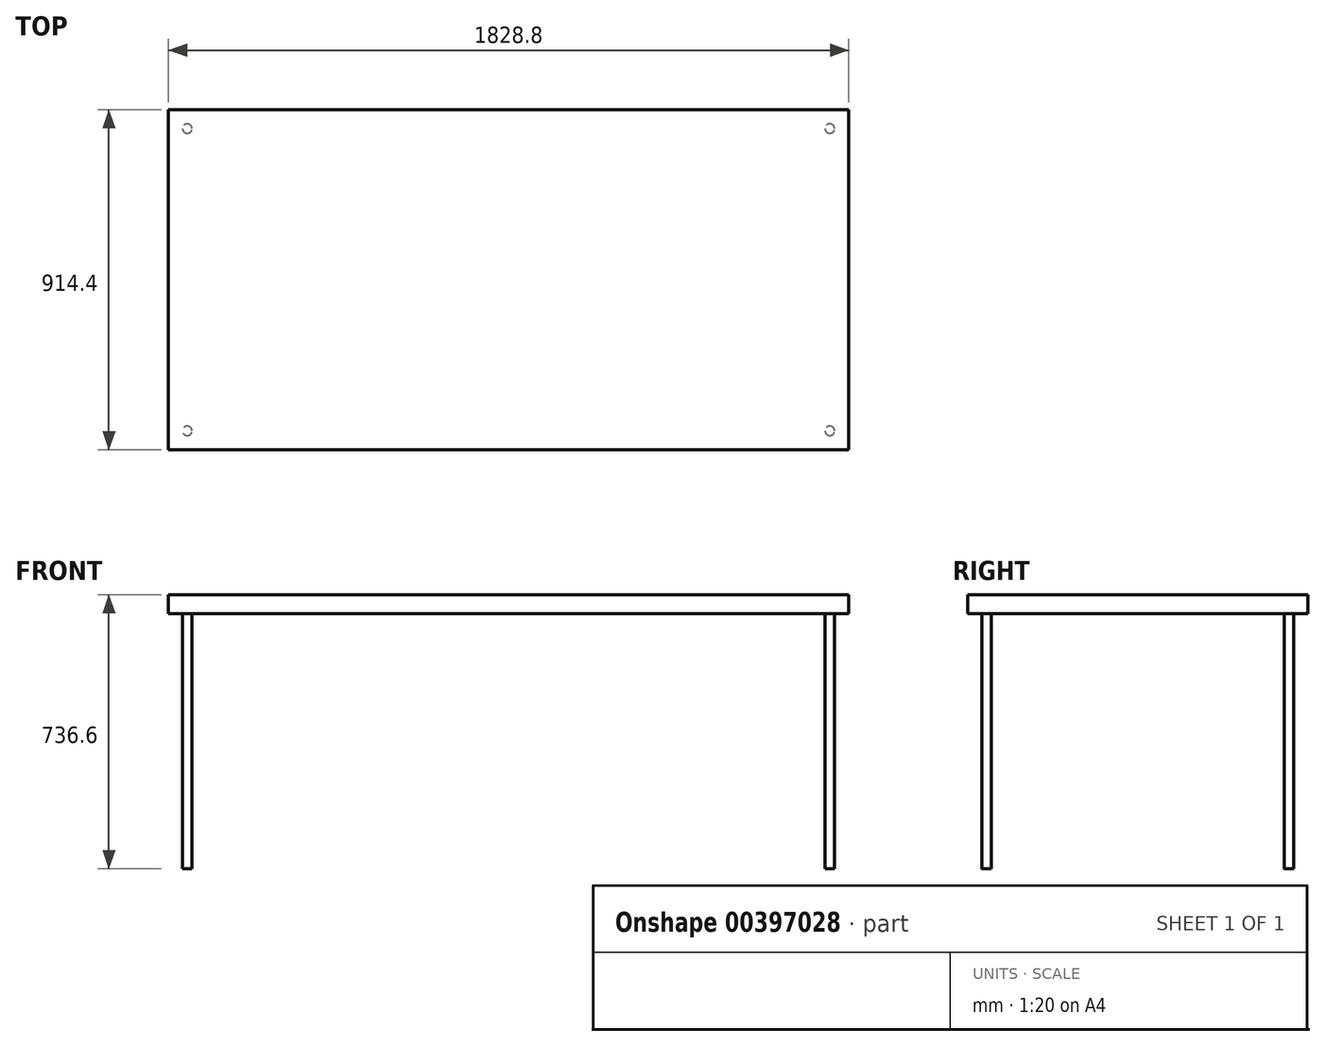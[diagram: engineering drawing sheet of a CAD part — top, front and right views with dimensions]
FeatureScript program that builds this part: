
annotation { "Feature Type Name" : "Feature", "Feature Type Description" : "" }
export const myFeature = defineFeature(function(context is Context, id is Id, definition is map)
    precondition{}
    {
        {
            var Q0;
            Q0=qCreatedBy(makeId("Top.planeOp"),FACE);
            var sketch = newSketch(context, id + "F0", { "sketchPlane" : qUnion([Q0])});
            skLineSegment(sketch, "E0.bottom", {"start": v(-914.4, -457.2) * mm, "end": v(914.4, -457.2) * mm});
            skLineSegment(sketch, "E0.top", {"start": v(-914.4, 457.2) * mm, "end": v(914.4, 457.2) * mm});
            skLineSegment(sketch, "E0.left", {"start": v(-914.4, -457.2) * mm, "end": v(-914.4, 457.2) * mm});
            skLineSegment(sketch, "E0.right", {"start": v(914.4, -457.2) * mm, "end": v(914.4, 457.2) * mm});
            skLineSegment(sketch, "E1", {"start": v(0, 457.2) * mm, "end": v(0, -457.2) * mm, "construction": true});
            skSolve(sketch);
        }
        {
            var Q0;
            Q0=qSketchRegion(id+"F0",true);
            extrude(context, id + "F1", {"entities" : qUnion([Q0]), "depth" : 50.8 * mm});
        }
        {
            var Q0;
            Q0=makeQuery(id+"F1.opExtrude","CAP_FACE",FACE,{"disambiguationData":[OSD([sQuery(id+"F0.wireOp",EDGE,"E0.bottom"),sQuery(id+"F0.wireOp",EDGE,"E0.top"),sQuery(id+"F0.wireOp",EDGE,"E0.left"),sQuery(id+"F0.wireOp",EDGE,"E0.right")])],"isStart":true});
            var sketch = newSketch(context, id + "F2", { "sketchPlane" : qUnion([Q0])});
            skCircle(sketch, "E2", {"center": v(-863.6, 406.4) * mm, "radius": 12.7 * mm});
            skCircle(sketch, "E3", {"center": v(-863.6, -406.4) * mm, "radius": 12.7 * mm});
            skCircle(sketch, "E4", {"center": v(863.6, -406.4) * mm, "radius": 12.7 * mm});
            skCircle(sketch, "E5", {"center": v(863.6, 406.4) * mm, "radius": 12.7 * mm});
            skSolve(sketch);
        }
        {
            var Q0;
            Q0=qSketchRegion(id+"F2",true);
            extrude(context, id + "F3", {"entities" : qUnion([Q0]), "operationType" : NewBodyOperationType.ADD, "depth" : 685.8 * mm});
        }
    });
